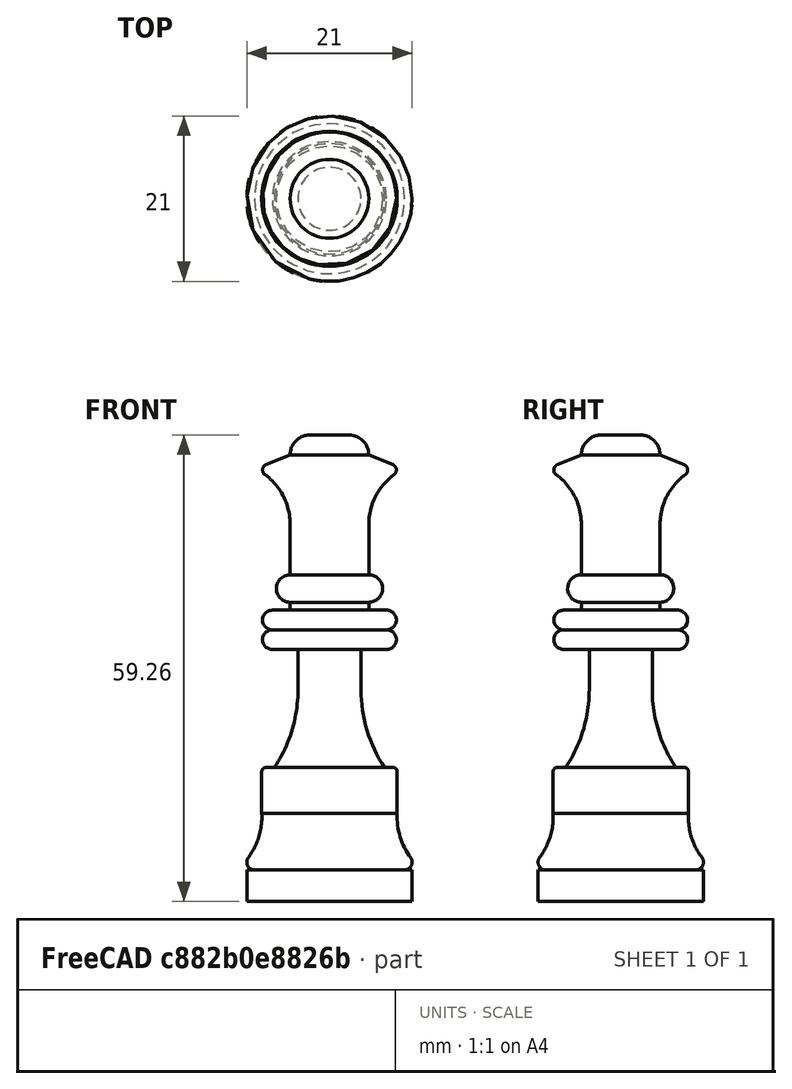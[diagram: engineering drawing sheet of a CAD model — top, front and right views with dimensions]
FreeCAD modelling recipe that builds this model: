
FCSTD DOCUMENT  (FreeCAD 1.0R39109 (Git))
Label: 1
License: All rights reserved
LicenseURL: https://en.wikipedia.org/wiki/All_rights_reserved
objects: Sketcher::SketchObject×1, PartDesign::Revolution×1, PartDesign::Body×1
note: 6 computed .brp shape members not serialized (recipe doc carries the construction recipe); baked Part::Feature solids carry a one-line shape summary decoded from their .brp

FEATURE [Sketcher::SketchObject] Sketch
  ArcFitTolerance = 1e-06
  AttachmentSupport = -> [XZ_Plane]
  FullyConstrained = false
  MakeInternals = false
  MapMode = 5
  Placement = pos=(0,0,0) rot=(1,0,0;1.5708rad)
  sketch-geometry (26):
    g0: LineSegment StartX=0 StartY=0 StartZ=0 EndX=10.5 EndY=0 EndZ=0
    g1: LineSegment StartX=10.5 StartY=0 StartZ=0 EndX=10.5 EndY=4 EndZ=0
    g2: LineSegment StartX=10.5 StartY=4 StartZ=0 EndX=9.52245 EndY=4 EndZ=0
    g3: ArcOfCircle CenterX=9.52245 CenterY=4.97755 CenterZ=0 NormalX=0 NormalY=0 NormalZ=1 AngleXU=0 Radius=0.977547 StartAngle=4.71239 EndAngle=6.92114
    g4: LineSegment StartX=8.6 StartY=11.1662 StartZ=0 EndX=8.6 EndY=16.5 EndZ=0
    g5: ArcOfCircle CenterX=17.3214 CenterY=10.7594 CenterZ=0 NormalX=0 NormalY=0 NormalZ=1 AngleXU=0 Radius=8.73092 StartAngle=3.09498 EndAngle=3.77954
    g6: ArcOfCircle CenterX=8.1 CenterY=16.5 CenterZ=0 NormalX=0 NormalY=0 NormalZ=1 AngleXU=0 Radius=0.5 StartAngle=1e-15 EndAngle=1.5708
    g7: GeomPoint [constr] X=8.6 Y=17 Z=0
    g8: ArcOfCircle CenterX=21.8675 CenterY=26.9098 CenterZ=0 NormalX=0 NormalY=0 NormalZ=1 AngleXU=0 Radius=17.8675 StartAngle=3.14159 EndAngle=3.72951
    g9: LineSegment StartX=4 StartY=26.9098 StartZ=0 EndX=4 EndY=32 EndZ=0
    g10: LineSegment StartX=7 StartY=17 StartZ=0 EndX=8.1 EndY=17 EndZ=0
    g11: LineSegment [constr] StartX=8.5 StartY=32.9141 StartZ=0 EndX=8.5 EndY=43.9755 EndZ=0
    g12: ArcOfCircle CenterX=7.25 CenterY=33.25 CenterZ=0 NormalX=0 NormalY=0 NormalZ=1 AngleXU=0 Radius=1.25 StartAngle=4.71239 EndAngle=7.85398
    g13: ArcOfCircle CenterX=7.25 CenterY=35.75 CenterZ=0 NormalX=0 NormalY=0 NormalZ=1 AngleXU=0 Radius=1.25 StartAngle=4.71239 EndAngle=7.85398
    g14: LineSegment StartX=4 StartY=32 StartZ=0 EndX=7.25 EndY=32 EndZ=0
    g15: LineSegment StartX=7.25 StartY=37 StartZ=0 EndX=5 EndY=37 EndZ=0
    g16: LineSegment StartX=5 StartY=37 StartZ=0 EndX=5 EndY=38 EndZ=0
    g17: ArcOfCircle CenterX=5 CenterY=39.75 CenterZ=0 NormalX=0 NormalY=0 NormalZ=1 AngleXU=0 Radius=1.75 StartAngle=4.71239 EndAngle=7.85398
    g18: LineSegment StartX=5 StartY=41.5 StartZ=0 EndX=5 EndY=47.8949 EndZ=0
    g19: LineSegment [constr] StartX=0 StartY=56.72 StartZ=0 EndX=8.5 EndY=56.72 EndZ=0
    g20: ArcOfCircle CenterX=2.46 CenterY=56.72 CenterZ=0 NormalX=0 NormalY=0 NormalZ=1 AngleXU=0 Radius=2.54 StartAngle=-9e-16 EndAngle=1.5708
    g21: LineSegment StartX=2.46 StartY=59.26 StartZ=0 EndX=0 EndY=59.26 EndZ=0
    g22: ArcOfCircle CenterX=12.8491 CenterY=47.8949 CenterZ=0 NormalX=0 NormalY=0 NormalZ=1 AngleXU=0 Radius=7.84912 StartAngle=2.20435 EndAngle=3.14159
    g23: LineSegment StartX=5 StartY=56.72 StartZ=0 EndX=8.04474 EndY=55.4847 EndZ=0
    g24: ArcOfCircle CenterX=7.77048 CenterY=54.8087 CenterZ=0 NormalX=0 NormalY=0 NormalZ=1 AngleXU=0 Radius=0.729516 StartAngle=5.34594 EndAngle=7.46856
    g25: LineSegment StartX=0 StartY=59.26 StartZ=0 EndX=0 EndY=0 EndZ=0
  constraints (75):
    c: Distance(g0) = 10.5
    c: Coincident(g0,g-1)
    c: PointOnObject(g0,g-1)
    c: Distance(g1) = 4
    c: Coincident(g1,g0)
    c: Vertical(g1)
    c: Coincident(g2,g1)
    c: Horizontal(g2)
    c: Tangent(g3,g1)
    c: Vertical(g4)
    c: Tangent(g3,g5) = 1.5708
    c: Coincident(g5,g4)
    c: Distance(g7,g2) = 13
    c: Distance(g7,g-2) = 8.6
    c: Block(g5)
    c: Tangent(g2,g3) = 1.5708
    c: PointOnObject(g7,g4)
    c: Tangent(g4,g6) = -1.5708
    c: Radius(g6) = 0.5
    c: Vertical(g9)
    c: Tangent(g9,g8) = 1.5708
    c: Distance(g8,g-2) = 7
    c: Distance(g8,g-2) = 4
    c: Coincident(g10,g8)
    c: Tangent(g10,g6) = 1.5708
    c: Horizontal(g10)
    c: Distance(g6,g2) = 13
    c: Distance(g9,g10) = 15
    c: Block(g8)
    c: Vertical(g11)
    c: Diameter(g12) = 2.5
    c: Diameter(g13) = 2.5
    c: Tangent(g12,g11)
    c: Distance(g11,g-2) = 8.5
    c: Tangent(g13,g11)
    c: Coincident(g14,g9)
    c: Horizontal(g14)
    c: Tangent(g12,g14) = -1.5708
    c: Horizontal(g15)
    c: Distance(g15,g-2) = 5
    c: Vertical(g15,g12)
    c: Coincident(g13,g15)
    c: Tangent(g13,g12) = 1.5708
    c: Distance(g16) = 1
    c: Coincident(g16,g15)
    c: Vertical(g16)
    c: Diameter(g17) = 3.5
    c: Vertical(g18)
    c: Coincident(g17,g18)
    c: Coincident(g17,g16)
    c: Vertical(g17,g17)
    c: Vertical(g17,g16)
    c: Distance(g19) = 8.5
    c: PointOnObject(g19,g-2)
    c: Horizontal(g19)
    c: Radius(g20) = 2.54
    c: Angle(g20) = 1.5708
    c: Distance(g20,g-2) = 5
    c: Horizontal(g20,g20)
    c: Coincident(g21,g20)
    c: Horizontal(g21)
    c: PointOnObject(g20,g19)
    c: Distance(g17,g19) = 15.22
    c: PointOnObject(g21,g-2)
    c: Coincident(g23,g20)
    c: Tangent(g22,g18) = 1.5708
    c: Tangent(g23,g24) = 1.5708
    c: Tangent(g22,g24) = 1.5708
    c: Tangent(g24,g11)
    c: Block(g22)
    c: Block(g18)
    c: Block(g24)
    c: Block(g23)
    c: Coincident(g25,g21)
    c: Coincident(g25,g0)
FEATURE [PartDesign::Revolution] Revolution
  Angle = 360
  Angle2 = 60
  Axis = (0,2e-16,1)
  Base = (0,0,0)
  Placement = pos=(0,0,0) rot=(1,0,0;1.5708rad)
  Profile = -> Sketch
  ReferenceAxis = -> Sketch [V_Axis]
  Refine = true
  Reversed = true
  Suppressed = false
  Type = 0
FEATURE [PartDesign::Body] Body  label="Тело"
  AllowCompound = false
  Group = -> [Sketch,Revolution]
  Origin = -> Origin
  Tip = -> Revolution
